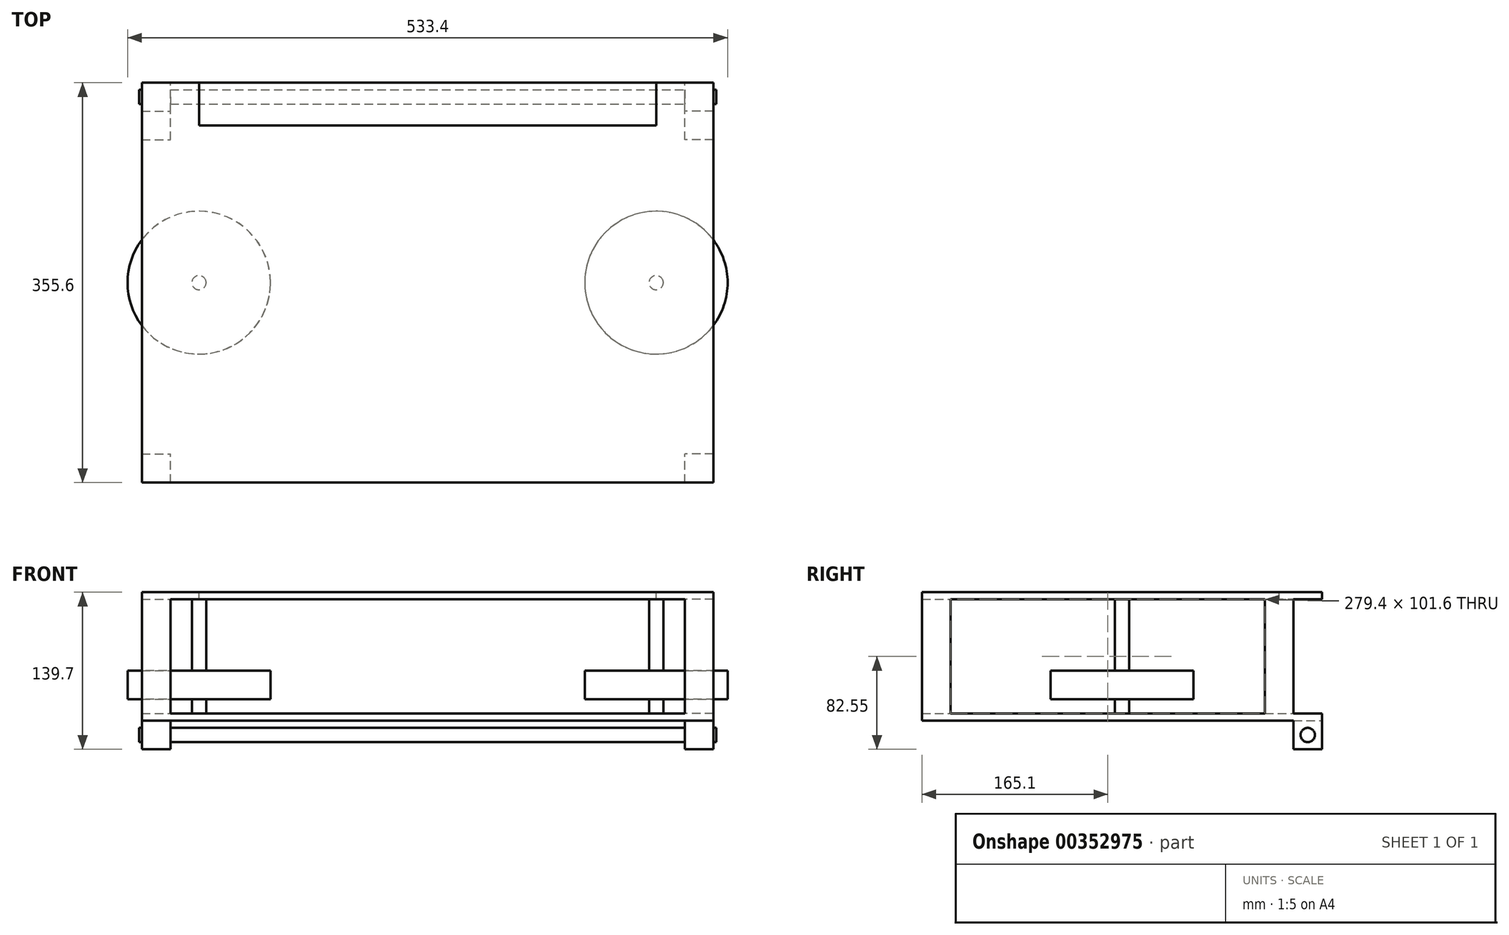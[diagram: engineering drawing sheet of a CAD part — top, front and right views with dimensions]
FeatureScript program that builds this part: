
annotation { "Feature Type Name" : "Feature", "Feature Type Description" : "" }
export const myFeature = defineFeature(function(context is Context, id is Id, definition is map)
    precondition{}
    {
        {
            var Q0;
            Q0=qCreatedBy(makeId("Top.planeOp"),FACE);
            var sketch = newSketch(context, id + "F0", { "sketchPlane" : qUnion([Q0])});
            skLineSegment(sketch, "E0.bottom", {"start": v(254, -177.8) * mm, "end": v(-254, -177.8) * mm});
            skLineSegment(sketch, "E0.top", {"start": v(254, 177.8) * mm, "end": v(-254, 177.8) * mm});
            skLineSegment(sketch, "E0.left", {"start": v(254, -177.8) * mm, "end": v(254, 177.8) * mm});
            skLineSegment(sketch, "E0.right", {"start": v(-254, -177.8) * mm, "end": v(-254, 177.8) * mm});
            skPoint(sketch, "E0.middle", {"position": v(0, 0) * mm});
            skSolve(sketch);
        }
        {
            var Q0;
            Q0 = qSketchRegion(id + "F0", true);
            extrude(context, id + "F1", {"entities" : qUnion([Q0]), "depth" : 6.35 * mm});
        }
        {
            var Q0;
            Q0=makeQuery(id+"F1.opExtrude","SWEPT_FACE",FACE,{"disambiguationData":[OSD([sQuery(id+"F0.wireOp",EDGE,"E0.left")])]});
            var sketch = newSketch(context, id + "F2", { "sketchPlane" : qUnion([Q0])});
            skLineSegment(sketch, "E1.bottom", {"start": v(177.8, 0) * mm, "end": v(152.4, 0) * mm});
            skLineSegment(sketch, "E1.top", {"start": v(177.8, -25.4) * mm, "end": v(152.4, -25.4) * mm});
            skLineSegment(sketch, "E1.left", {"start": v(177.8, 0) * mm, "end": v(177.8, -25.4) * mm});
            skLineSegment(sketch, "E1.right", {"start": v(152.4, 0) * mm, "end": v(152.4, -25.4) * mm});
            skSolve(sketch);
        }
        {
            var Q0;
            Q0 = qSketchRegion(id + "F2", true);
            extrude(context, id + "F3", {"entities" : qUnion([Q0]), "operationType" : NewBodyOperationType.ADD, "oppositeDirection" : true, "depth" : 25.4 * mm});
        }
        {
            var Q0;
            Q0=makeQuery(id+"F1.opExtrude","SWEPT_FACE",FACE,{"disambiguationData":[OSD([sQuery(id+"F0.wireOp",EDGE,"E0.right")])]});
            var sketch = newSketch(context, id + "F4", { "sketchPlane" : qUnion([Q0])});
            skLineSegment(sketch, "E2.bottom", {"start": v(-177.8, 0) * mm, "end": v(-152.4, 0) * mm});
            skLineSegment(sketch, "E2.top", {"start": v(-177.8, -25.4) * mm, "end": v(-152.4, -25.4) * mm});
            skLineSegment(sketch, "E2.left", {"start": v(-177.8, 0) * mm, "end": v(-177.8, -25.4) * mm});
            skLineSegment(sketch, "E2.right", {"start": v(-152.4, 0) * mm, "end": v(-152.4, -25.4) * mm});
            skSolve(sketch);
        }
        {
            var Q0;
            Q0=makeQuery(id+"F4.imprint","IMPRINT",FACE,{"disambiguationData":[TD([[makeQuery(id+"F4.imprint","IMPRINT",EDGE,{"derivedFrom":sQuery(id+"F4.wireOp",EDGE,"E2.bottom")}),1.0]])]});
            extrude(context, id + "F5", {"entities" : qUnion([Q0]), "operationType" : NewBodyOperationType.ADD, "oppositeDirection" : true, "depth" : 25.4 * mm});
        }
        {
            var Q0;
            Q0=makeQuery(id+"F5.boolean.opBoolean","MERGE",FACE,{"derivedFrom":[makeQuery(id+"F1.opExtrude","SWEPT_FACE",FACE,{"disambiguationData":[OSD([sQuery(id+"F0.wireOp",EDGE,"E0.right")])]}),makeQuery(id+"F5.opExtrude","CAP_FACE",FACE,{"disambiguationData":[OSD([sQuery(id+"F4.wireOp",EDGE,"E2.bottom"),sQuery(id+"F4.wireOp",EDGE,"E2.top"),sQuery(id+"F4.wireOp",EDGE,"E2.left"),sQuery(id+"F4.wireOp",EDGE,"E2.right")])],"isStart":true})]});
            var sketch = newSketch(context, id + "F6", { "sketchPlane" : qUnion([Q0])});
            skCircle(sketch, "E3", {"center": v(-165.1, -12.7) * mm, "radius": 6.35 * mm});
            skSolve(sketch);
        }
        {
            var Q0;
            Q0 = qSketchRegion(id + "F6", true);
            extrude(context, id + "F7", {"entities" : qUnion([Q0]), "operationType" : NewBodyOperationType.ADD, "depth" : 2.54 * mm, "hasSecondDirection" : true, "secondDirectionOppositeDirection" : true, "secondDirectionDepth" : 510.54 * mm});
        }
        {
            var Q0;
            Q0=makeQuery(id+"F1.opExtrude","CAP_FACE",FACE,{"disambiguationData":[OSD([sQuery(id+"F0.wireOp",EDGE,"E0.bottom"),sQuery(id+"F0.wireOp",EDGE,"E0.top"),sQuery(id+"F0.wireOp",EDGE,"E0.left"),sQuery(id+"F0.wireOp",EDGE,"E0.right")])],"isStart":false});
            var sketch = newSketch(context, id + "F8", { "sketchPlane" : qUnion([Q0])});
            skLineSegment(sketch, "E4.bottom", {"start": v(254, -177.8) * mm, "end": v(228.6, -177.8) * mm});
            skLineSegment(sketch, "E4.top", {"start": v(254, -152.4) * mm, "end": v(228.6, -152.4) * mm});
            skLineSegment(sketch, "E4.left", {"start": v(254, -177.8) * mm, "end": v(254, -152.4) * mm});
            skLineSegment(sketch, "E4.right", {"start": v(228.6, -177.8) * mm, "end": v(228.6, -152.4) * mm});
            skLineSegment(sketch, "E5.bottom", {"start": v(-254, -177.8) * mm, "end": v(-228.6, -177.8) * mm});
            skLineSegment(sketch, "E5.top", {"start": v(-254, -152.4) * mm, "end": v(-228.6, -152.4) * mm});
            skLineSegment(sketch, "E5.left", {"start": v(-254, -177.8) * mm, "end": v(-254, -152.4) * mm});
            skLineSegment(sketch, "E5.right", {"start": v(-228.6, -177.8) * mm, "end": v(-228.6, -152.4) * mm});
            skLineSegment(sketch, "E6.bottom", {"start": v(254, 127) * mm, "end": v(228.6, 127) * mm});
            skLineSegment(sketch, "E6.top", {"start": v(254, 152.4) * mm, "end": v(228.6, 152.4) * mm});
            skLineSegment(sketch, "E6.left", {"start": v(254, 127) * mm, "end": v(254, 152.4) * mm});
            skLineSegment(sketch, "E6.right", {"start": v(228.6, 127) * mm, "end": v(228.6, 152.4) * mm});
            skLineSegment(sketch, "E7.bottom", {"start": v(-254, 127) * mm, "end": v(-228.6, 127) * mm});
            skLineSegment(sketch, "E7.top", {"start": v(-254, 152.4) * mm, "end": v(-228.6, 152.4) * mm});
            skLineSegment(sketch, "E7.left", {"start": v(-254, 127) * mm, "end": v(-254, 152.4) * mm});
            skLineSegment(sketch, "E7.right", {"start": v(-228.6, 127) * mm, "end": v(-228.6, 152.4) * mm});
            skSolve(sketch);
        }
        {
            var Q0;
            Q0 = qSketchRegion(id + "F8", true);
            extrude(context, id + "F9", {"entities" : qUnion([Q0]), "operationType" : NewBodyOperationType.ADD, "depth" : 101.6 * mm});
        }
        {
            var Q0;
            Q0=makeQuery(id+"F9.opExtrude","CAP_FACE",FACE,{"disambiguationData":[OSD([sQuery(id+"F8.wireOp",EDGE,"E5.bottom"),sQuery(id+"F8.wireOp",EDGE,"E5.top"),sQuery(id+"F8.wireOp",EDGE,"E5.left"),sQuery(id+"F8.wireOp",EDGE,"E5.right")])],"isStart":false});
            var sketch = newSketch(context, id + "F10", { "sketchPlane" : qUnion([Q0])});
            skLineSegment(sketch, "E8.bottom", {"start": v(-254, -177.8) * mm, "end": v(254, -177.8) * mm});
            skLineSegment(sketch, "E8.top", {"start": v(-254, 177.8) * mm, "end": v(254, 177.8) * mm});
            skLineSegment(sketch, "E8.left", {"start": v(-254, -177.8) * mm, "end": v(-254, 177.8) * mm});
            skLineSegment(sketch, "E8.right", {"start": v(254, -177.8) * mm, "end": v(254, 177.8) * mm});
            skSolve(sketch);
        }
        {
            var Q0;
            Q0 = qSketchRegion(id + "F10", true);
            extrude(context, id + "F11", {"entities" : qUnion([Q0]), "operationType" : NewBodyOperationType.ADD, "depth" : 6.35 * mm});
        }
        {
            var Q0;
            Q0=makeQuery(id+"F1.opExtrude","CAP_FACE",FACE,{"disambiguationData":[OSD([sQuery(id+"F0.wireOp",EDGE,"E0.bottom"),sQuery(id+"F0.wireOp",EDGE,"E0.top"),sQuery(id+"F0.wireOp",EDGE,"E0.left"),sQuery(id+"F0.wireOp",EDGE,"E0.right")])],"isStart":false});
            var sketch = newSketch(context, id + "F12", { "sketchPlane" : qUnion([Q0])});
            skCircle(sketch, "E9", {"center": v(-203.2, 0) * mm, "radius": 63.5 * mm});
            skCircle(sketch, "E10", {"center": v(203.2, 0) * mm, "radius": 63.5 * mm});
            skSolve(sketch);
        }
        {
            var Q0;
            Q0 = qSketchRegion(id + "F12", true);
            extrude(context, id + "F13", {"entities" : qUnion([Q0]), "depth" : 38.1 * mm, "hasSecondDirection" : true, "secondDirectionOppositeDirection" : false, "secondDirectionDepth" : 12.7 * mm});
        }
        {
            var Q0;
            Q0=makeQuery(id+"F12.imprint","IMPRINT",FACE,{"disambiguationData":[TD([[makeQuery(id+"F12.imprint","IMPRINT",EDGE,{"derivedFrom":sQuery(id+"F12.wireOp",EDGE,"E9")}),-1.0]])]});
            var sketch = newSketch(context, id + "F14", { "sketchPlane" : qUnion([Q0])});
            skCircle(sketch, "E11", {"center": v(203.2, 0) * mm, "radius": 6.35 * mm});
            skCircle(sketch, "E12", {"center": v(-203.2, 0) * mm, "radius": 6.35 * mm});
            skSolve(sketch);
        }
        {
            var Q0;
            Q0 = qSketchRegion(id + "F14", true);
            extrude(context, id + "F15", {"entities" : qUnion([Q0]), "operationType" : NewBodyOperationType.ADD, "depth" : 101.6 * mm});
        }
        {
            var Q0;
            Q0=makeQuery(id+"F11.opExtrude","CAP_FACE",FACE,{"disambiguationData":[OSD([sQuery(id+"F10.wireOp",EDGE,"E8.bottom"),sQuery(id+"F10.wireOp",EDGE,"E8.top"),sQuery(id+"F10.wireOp",EDGE,"E8.left"),sQuery(id+"F10.wireOp",EDGE,"E8.right")])],"isStart":false});
            var sketch = newSketch(context, id + "F16", { "sketchPlane" : qUnion([Q0])});
            skLineSegment(sketch, "E13.bottom", {"start": v(-203.2, 177.8) * mm, "end": v(203.2, 177.8) * mm});
            skLineSegment(sketch, "E13.top", {"start": v(-203.2, 139.7) * mm, "end": v(203.2, 139.7) * mm});
            skLineSegment(sketch, "E13.left", {"start": v(-203.2, 177.8) * mm, "end": v(-203.2, 139.7) * mm});
            skLineSegment(sketch, "E13.right", {"start": v(203.2, 177.8) * mm, "end": v(203.2, 139.7) * mm});
            skSolve(sketch);
        }
        {
            var Q0;
            Q0 = qSketchRegion(id + "F16", true);
            extrude(context, id + "F17", {"entities" : qUnion([Q0]), "operationType" : NewBodyOperationType.REMOVE, "oppositeDirection" : true, "depth" : 6.35 * mm});
        }
    });
